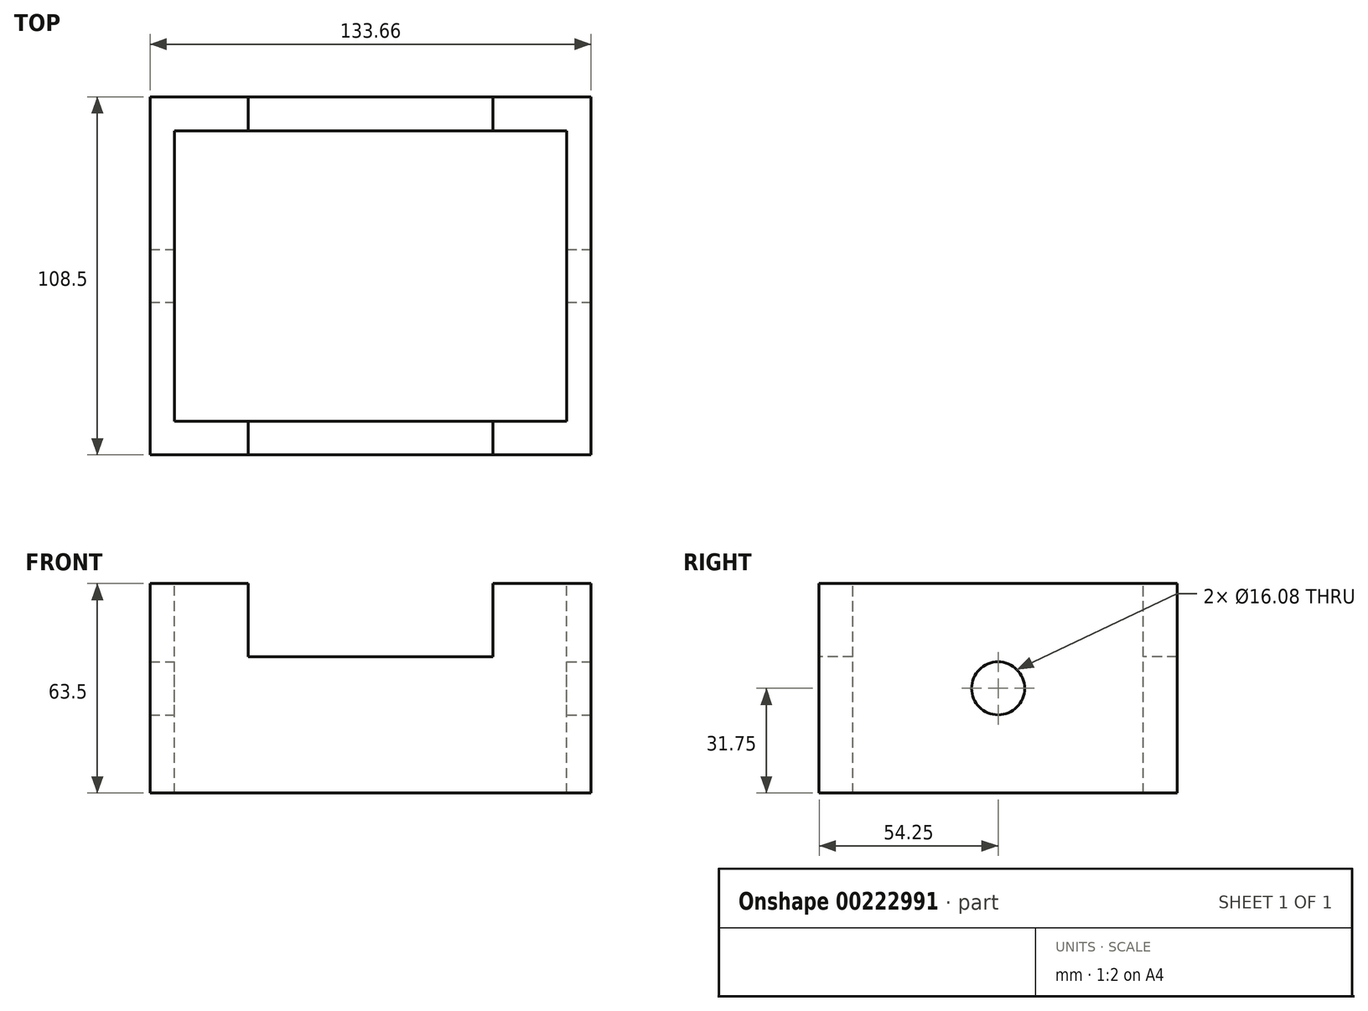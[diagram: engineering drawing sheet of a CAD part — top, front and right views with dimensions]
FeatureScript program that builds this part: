
annotation { "Feature Type Name" : "Feature", "Feature Type Description" : "" }
export const myFeature = defineFeature(function(context is Context, id is Id, definition is map)
    precondition{}
    {
        {
            var Q0;
            Q0=qCreatedBy(makeId("Top.planeOp"),FACE);
            var sketch = newSketch(context, id + "F0", { "sketchPlane" : qUnion([Q0])});
            skLineSegment(sketch, "E0.bottom", {"start": v(66.83, -54.25) * mm, "end": v(-66.83, -54.25) * mm});
            skLineSegment(sketch, "E0.top", {"start": v(66.83, 54.25) * mm, "end": v(-66.83, 54.25) * mm});
            skLineSegment(sketch, "E0.left", {"start": v(66.83, -54.25) * mm, "end": v(66.83, 54.25) * mm});
            skLineSegment(sketch, "E0.right", {"start": v(-66.83, -54.25) * mm, "end": v(-66.83, 54.25) * mm});
            skPoint(sketch, "E0.middle", {"position": v(0, 0) * mm});
            skSolve(sketch);
        }
        {
            var Q0;
            Q0 = qSketchRegion(id + "F0", true);
            extrude(context, id + "F1", {"entities" : qUnion([Q0]), "depth" : 63.5 * mm});
        }
        {
            var Q0;
            Q0=makeQuery(id+"F1.opExtrude","SWEPT_FACE",FACE,{"disambiguationData":[OSD([sQuery(id+"F0.wireOp",EDGE,"E0.left")])]});
            var sketch = newSketch(context, id + "F2", { "sketchPlane" : qUnion([Q0])});
            skCircle(sketch, "E1", {"center": v(0, 31.75) * mm, "radius": 8.04 * mm});
            skPoint(sketch, "E1.centerSnap0", {"position": v(-54.25, 31.75) * mm});
            skPoint(sketch, "E1.centerSnap1", {"position": v(0, 63.5) * mm});
            skSolve(sketch);
        }
        {
            var Q0;
            Q0 = qSketchRegion(id + "F2", true);
            extrude(context, id + "F3", {"entities" : qUnion([Q0]), "operationType" : NewBodyOperationType.REMOVE, "endBound" : BoundingType.THROUGH_ALL, "oppositeDirection" : true, "depth" : 25.4 * mm});
        }
        {
            var Q0;
            Q0=makeQuery(id+"F1.opExtrude","CAP_FACE",FACE,{"disambiguationData":[OSD([sQuery(id+"F0.wireOp",EDGE,"E0.bottom"),sQuery(id+"F0.wireOp",EDGE,"E0.top"),sQuery(id+"F0.wireOp",EDGE,"E0.left"),sQuery(id+"F0.wireOp",EDGE,"E0.right")])],"isStart":false});
            var sketch = newSketch(context, id + "F4", { "sketchPlane" : qUnion([Q0])});
            skLineSegment(sketch, "E2.bottom", {"start": v(59.44, -44.01) * mm, "end": v(-59.44, -44.01) * mm});
            skLineSegment(sketch, "E2.top", {"start": v(59.44, 44.01) * mm, "end": v(-59.44, 44.01) * mm});
            skLineSegment(sketch, "E2.left", {"start": v(59.44, -44.01) * mm, "end": v(59.44, 44.01) * mm});
            skLineSegment(sketch, "E2.right", {"start": v(-59.44, -44.01) * mm, "end": v(-59.44, 44.01) * mm});
            skPoint(sketch, "E2.middle", {"position": v(0, 0) * mm});
            skSolve(sketch);
        }
        {
            var Q0;
            Q0 = qSketchRegion(id + "F4", true);
            extrude(context, id + "F5", {"entities" : qUnion([Q0]), "operationType" : NewBodyOperationType.REMOVE, "endBound" : BoundingType.THROUGH_ALL, "oppositeDirection" : true, "depth" : 25.4 * mm});
        }
        {
            var Q0;
            Q0=makeQuery(id+"F1.opExtrude","SWEPT_FACE",FACE,{"disambiguationData":[OSD([sQuery(id+"F0.wireOp",EDGE,"E0.bottom")])]});
            var sketch = newSketch(context, id + "F6", { "sketchPlane" : qUnion([Q0])});
            skLineSegment(sketch, "E3.0", {"start": v(66.83, 63.5) * mm, "end": v(-66.83, 63.5) * mm});
            skLineSegment(sketch, "E4", {"start": v(-37.07, 63.5) * mm, "end": v(-37.07, 41.26) * mm});
            skLineSegment(sketch, "E5", {"start": v(-37.07, 41.26) * mm, "end": v(37.07, 41.26) * mm});
            skLineSegment(sketch, "E6", {"start": v(37.07, 41.26) * mm, "end": v(37.07, 63.5) * mm});
            skSolve(sketch);
        }
        {
            var Q0;
            Q0 = qSketchRegion(id + "F6", true);
            extrude(context, id + "F7", {"entities" : qUnion([Q0]), "operationType" : NewBodyOperationType.REMOVE, "endBound" : BoundingType.THROUGH_ALL, "oppositeDirection" : true, "depth" : 25.4 * mm});
        }
    });
